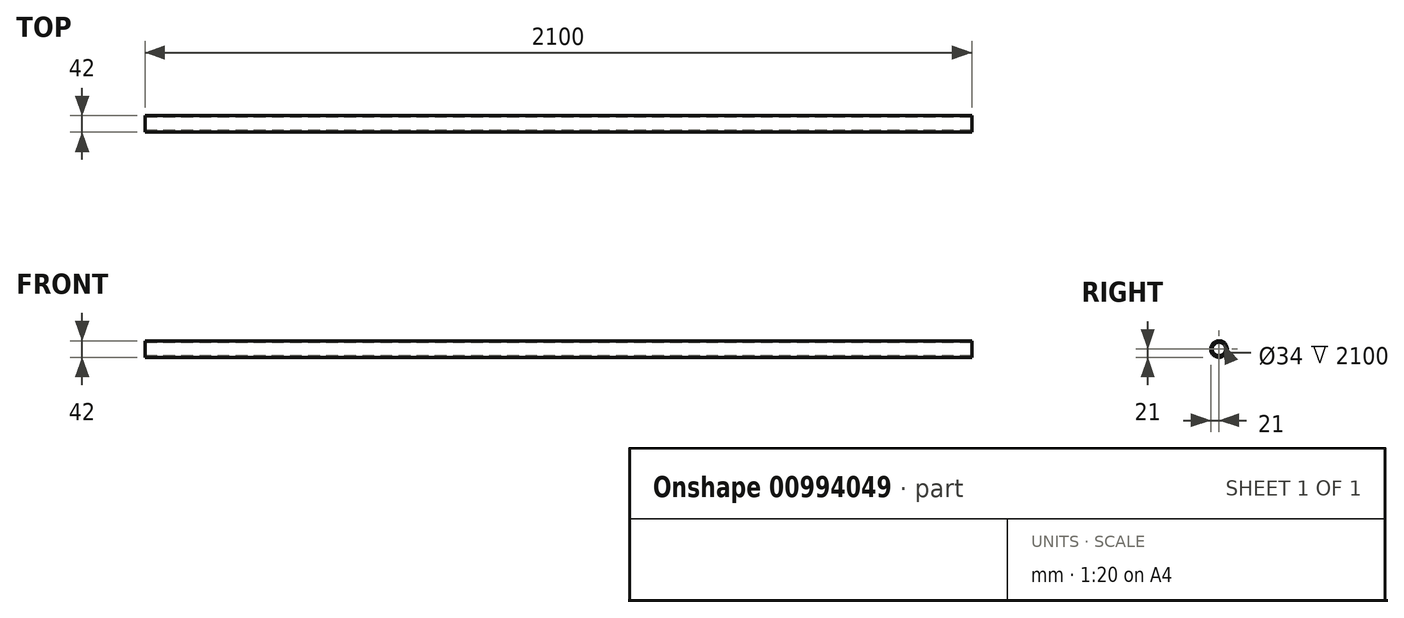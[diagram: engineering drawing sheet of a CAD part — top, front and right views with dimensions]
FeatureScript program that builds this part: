
annotation { "Feature Type Name" : "Feature", "Feature Type Description" : "" }
export const myFeature = defineFeature(function(context is Context, id is Id, definition is map)
    precondition{}
    {
        {
            var Q0;
            Q0=qCreatedBy(makeId("Right.planeOp"),FACE);
            var sketch = newSketch(context, id + "F0", { "sketchPlane" : qUnion([Q0])});
            skCircle(sketch, "E0", {"center": v(0, 0) * mm, "radius": 21 * mm});
            skCircle(sketch, "E1", {"center": v(0, 0) * mm, "radius": 17 * mm});
            skSolve(sketch);
        }
        {
            var Q0;
            Q0 = qSketchRegion(id + "F0", true);
            extrude(context, id + "F1", {"entities" : qUnion([Q0]), "endBound" : BoundingType.SYMMETRIC, "depth" : 2100 * mm, "offsetDistance" : 25 * mm});
        }
    });
